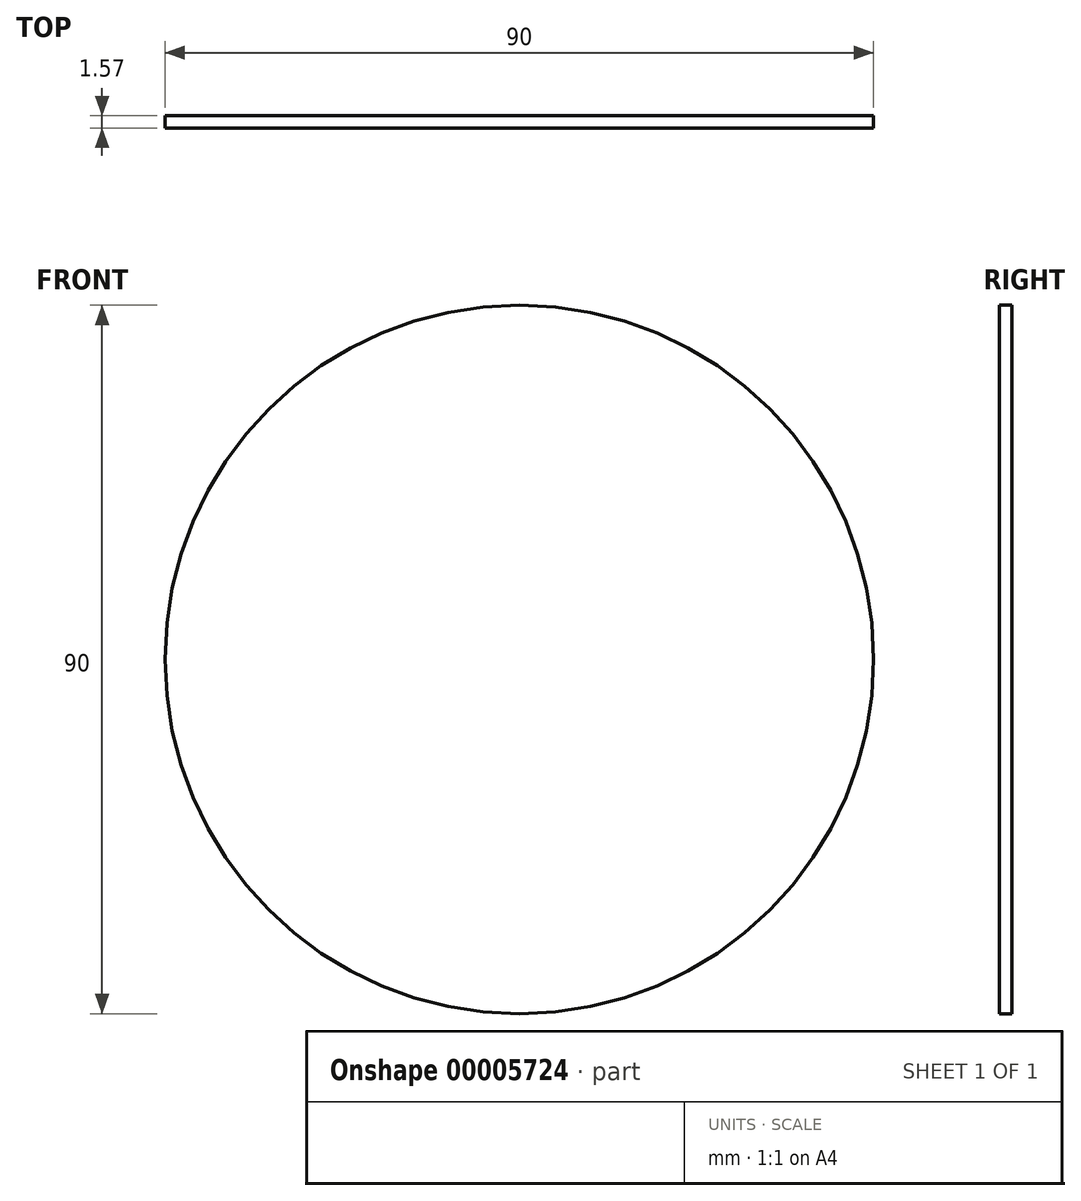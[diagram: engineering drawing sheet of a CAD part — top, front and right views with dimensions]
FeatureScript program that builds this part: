
annotation { "Feature Type Name" : "Feature", "Feature Type Description" : "" }
export const myFeature = defineFeature(function(context is Context, id is Id, definition is map)
    precondition{}
    {
        {
            var Q0;
            Q0=qCreatedBy(makeId("Front.planeOp"),FACE);
            var sketch = newSketch(context, id + "F0", { "sketchPlane" : qUnion([Q0])});
            skCircle(sketch, "E0", {"center": v(0, 0) * mm, "radius": 45 * mm});
            skSolve(sketch);
        }
        {
            var Q0;
            Q0=makeQuery(id+"F0.imprint","IMPRINT",FACE,{"disambiguationData":[TD([[makeQuery(id+"F0.imprint","IMPRINT",EDGE,{"derivedFrom":sQuery(id+"F0.wireOp",EDGE,"E0")}),1.0]])]});
            extrude(context, id + "F1", {"entities" : qUnion([Q0]), "depth" : 1.57 * mm});
        }
    });
